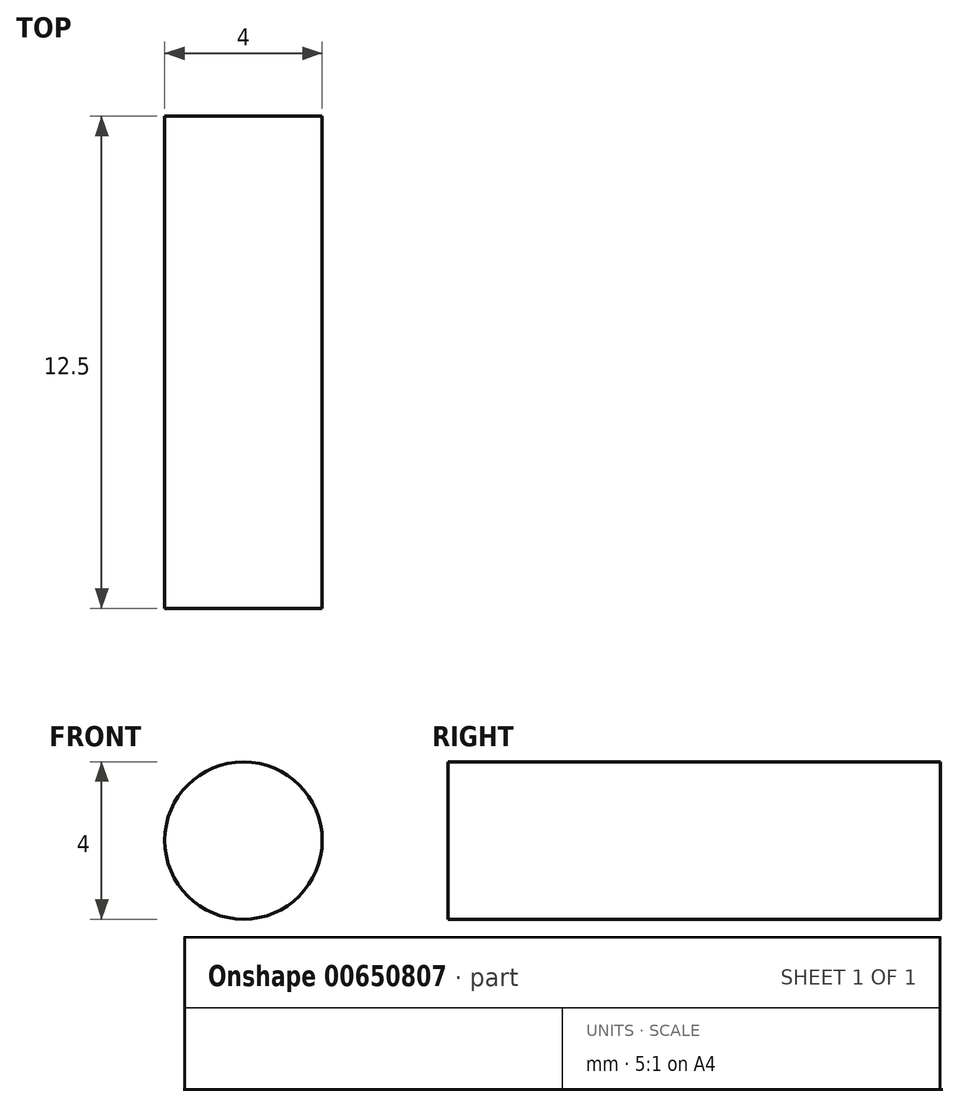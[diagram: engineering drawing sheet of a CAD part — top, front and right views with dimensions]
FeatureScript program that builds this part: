
annotation { "Feature Type Name" : "Feature", "Feature Type Description" : "" }
export const myFeature = defineFeature(function(context is Context, id is Id, definition is map)
    precondition{}
    {
        {
            var Q0;
            Q0=qCreatedBy(makeId("Front.planeOp"),FACE);
            var sketch = newSketch(context, id + "F0", { "sketchPlane" : qUnion([Q0])});
            skCircle(sketch, "E0", {"center": v(0, 0) * mm, "radius": 2 * mm});
            skSolve(sketch);
        }
        {
            var Q0;
            Q0=makeQuery(id+"F0.imprint","IMPRINT",FACE,{"disambiguationData":[TD([[makeQuery(id+"F0.imprint","IMPRINT",EDGE,{"derivedFrom":sQuery(id+"F0.wireOp",EDGE,"E0")}),1.0]])]});
            extrude(context, id + "F1", {"entities" : qUnion([Q0]), "endBound" : BoundingType.SYMMETRIC, "depth" : 12.5 * mm, "offsetDistance" : 25 * mm});
        }
    });
